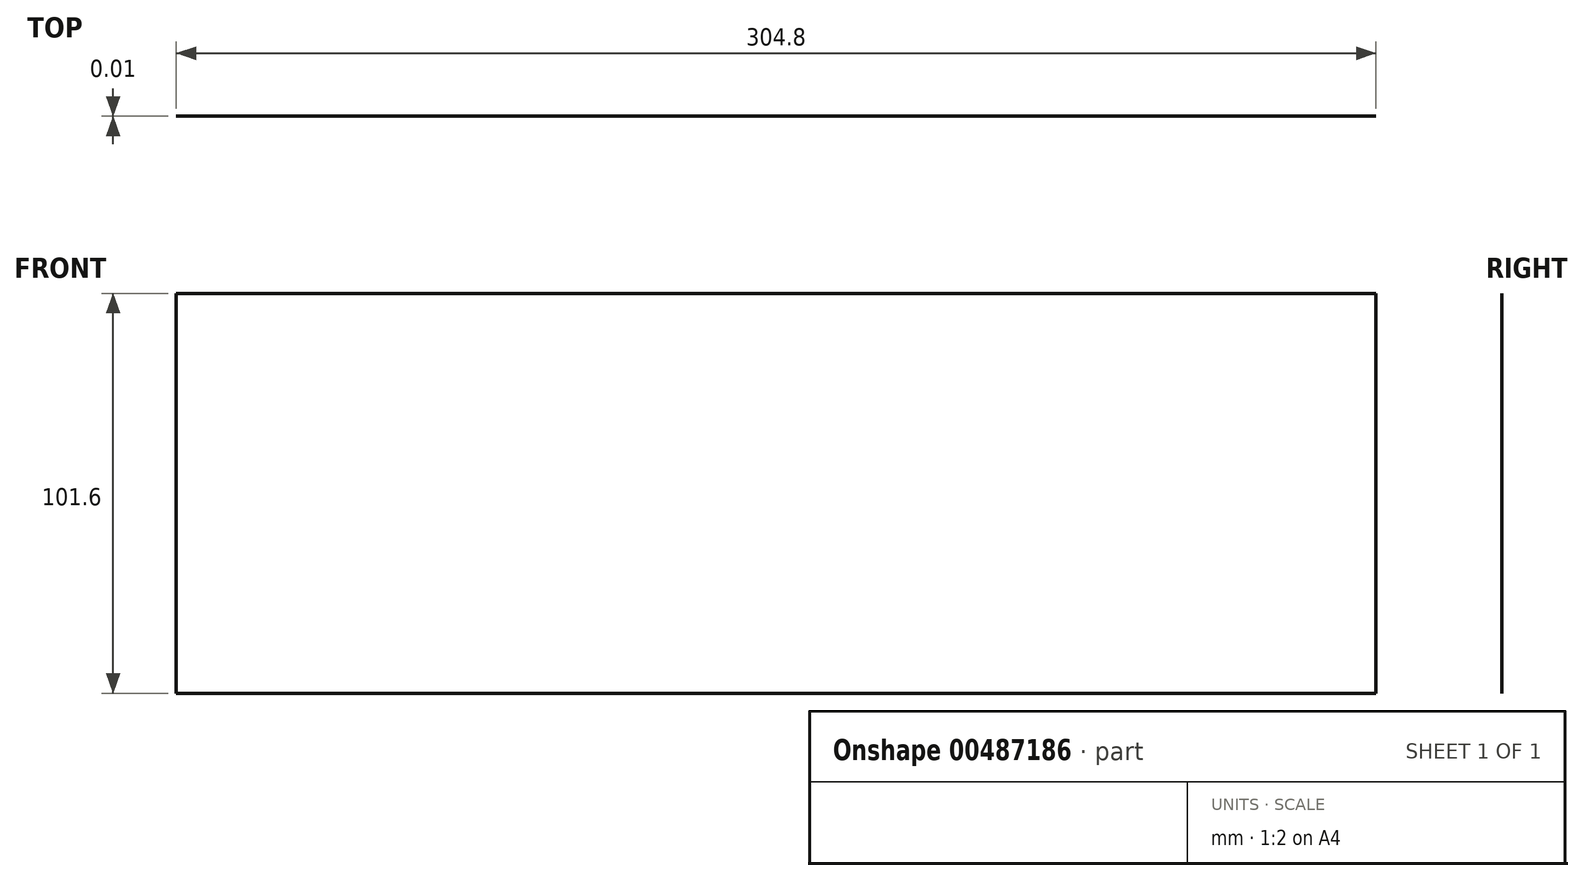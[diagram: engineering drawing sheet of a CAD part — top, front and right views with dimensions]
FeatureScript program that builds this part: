
annotation { "Feature Type Name" : "Feature", "Feature Type Description" : "" }
export const myFeature = defineFeature(function(context is Context, id is Id, definition is map)
    precondition{}
    {
        {
            var Q0;
            Q0=qCreatedBy(makeId("Front.planeOp"),FACE);
            var sketch = newSketch(context, id + "F0", { "sketchPlane" : qUnion([Q0])});
            skLineSegment(sketch, "E0.bottom", {"start": v(152.4, 50.8) * mm, "end": v(-152.4, 50.8) * mm});
            skLineSegment(sketch, "E0.top", {"start": v(152.4, -50.8) * mm, "end": v(-152.4, -50.8) * mm});
            skLineSegment(sketch, "E0.left", {"start": v(152.4, 50.8) * mm, "end": v(152.4, -50.8) * mm});
            skLineSegment(sketch, "E0.right", {"start": v(-152.4, 50.8) * mm, "end": v(-152.4, -50.8) * mm});
            skPoint(sketch, "E0.middle", {"position": v(0, 0) * mm});
            skSolve(sketch);
        }
        {
            var Q0;
            Q0 = qSketchRegion(id + "F0", true);
            extrude(context, id + "F1", {"entities" : qUnion([Q0]), "depth" : 1 / 101.6 * mm});
        }
    });
